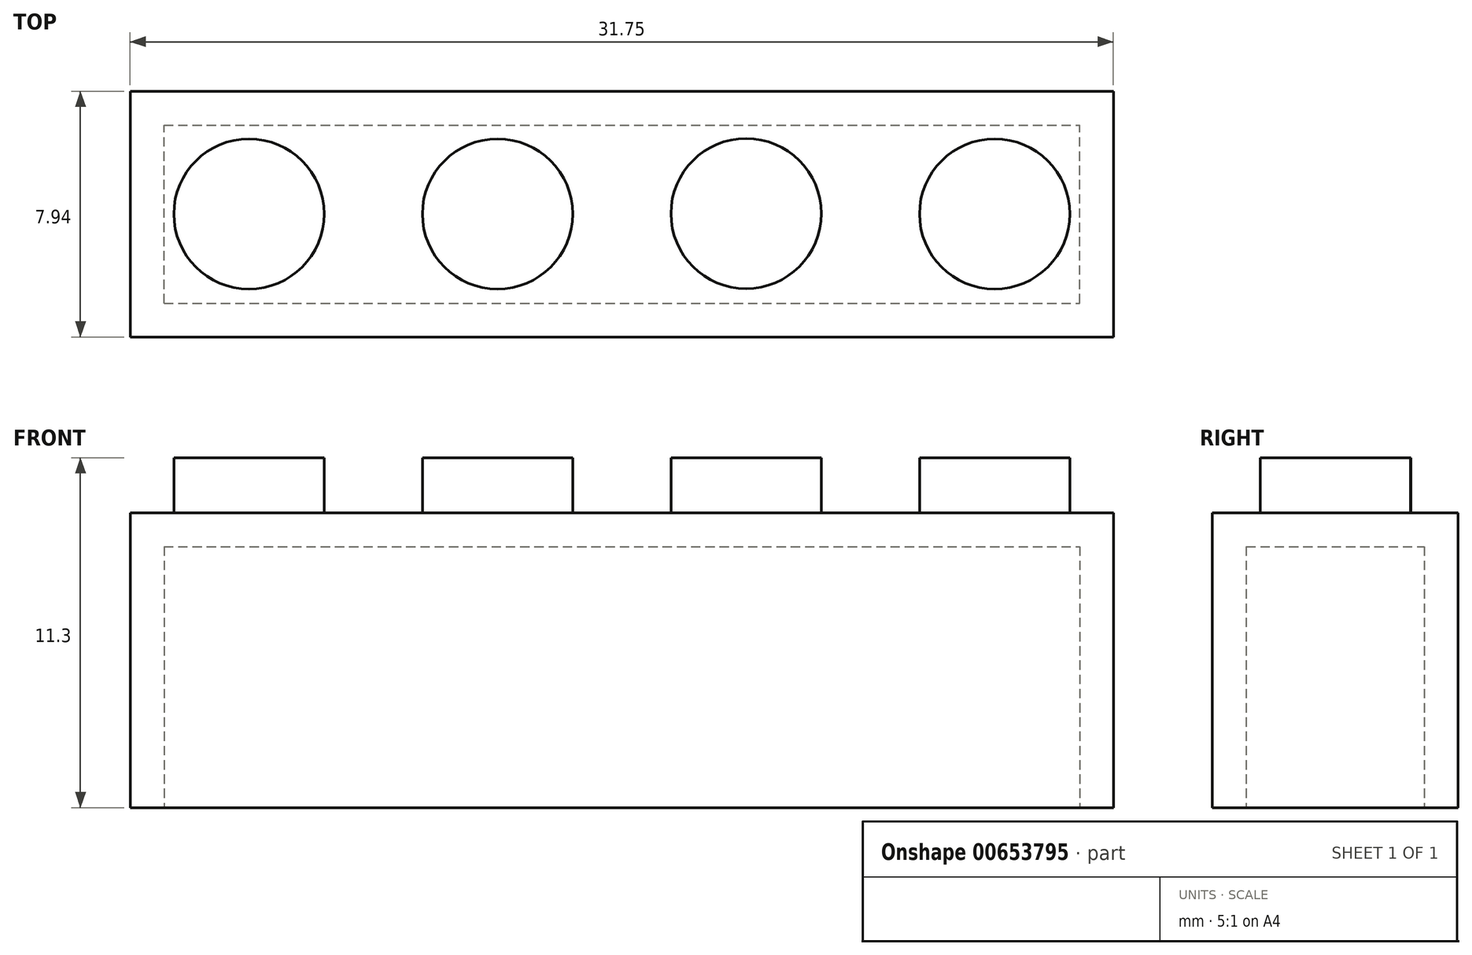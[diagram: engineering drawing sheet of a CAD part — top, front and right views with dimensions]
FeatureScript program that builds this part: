
annotation { "Feature Type Name" : "Feature", "Feature Type Description" : "" }
export const myFeature = defineFeature(function(context is Context, id is Id, definition is map)
    precondition{}
    {
        {
            var Q0;
            Q0=qCreatedBy(makeId("Top.planeOp"),FACE);
            var sketch = newSketch(context, id + "F0", { "sketchPlane" : qUnion([Q0])});
            skLineSegment(sketch, "E0.bottom", {"start": v(-30.69, 19.47) * mm, "end": v(1.06, 19.47) * mm});
            skLineSegment(sketch, "E0.top", {"start": v(-30.69, 11.53) * mm, "end": v(1.06, 11.53) * mm});
            skLineSegment(sketch, "E0.left", {"start": v(-30.69, 19.47) * mm, "end": v(-30.69, 11.53) * mm});
            skLineSegment(sketch, "E0.right", {"start": v(1.06, 19.47) * mm, "end": v(1.06, 11.53) * mm});
            skSolve(sketch);
        }
        {
            var Q0;
            Q0 = qSketchRegion(id + "F0", true);
            extrude(context, id + "F1", {"entities" : qUnion([Q0]), "depth" : 9.52 * mm, "offsetDistance" : 25.4 * mm});
        }
        {
            var Q0;
            Q0=makeQuery(id+"F1.opExtrude","CAP_FACE",FACE,{"disambiguationData":[OSD([sQuery(id+"F0.wireOp",EDGE,"E0.bottom"),sQuery(id+"F0.wireOp",EDGE,"E0.top"),sQuery(id+"F0.wireOp",EDGE,"E0.left"),sQuery(id+"F0.wireOp",EDGE,"E0.right")])],"isStart":false});
            var sketch = newSketch(context, id + "F2", { "sketchPlane" : qUnion([Q0])});
            skCircle(sketch, "E1", {"center": v(-26.85, 15.5) * mm, "radius": 2.43 * mm});
            skCircle(sketch, "E2", {"center": v(-18.83, 15.5) * mm, "radius": 2.43 * mm});
            skCircle(sketch, "E3", {"center": v(-10.8, 15.52) * mm, "radius": 2.43 * mm});
            skCircle(sketch, "E4", {"center": v(-2.77, 15.5) * mm, "radius": 2.43 * mm});
            skSolve(sketch);
        }
        {
            var Q0;
            Q0 = qSketchRegion(id + "F2", true);
            extrude(context, id + "F3", {"entities" : qUnion([Q0]), "operationType" : NewBodyOperationType.ADD, "depth" : 1.78 * mm, "offsetDistance" : 25.4 * mm});
        }
        {
            var Q0;
            Q0=makeQuery(id+"F1.opExtrude","CAP_FACE",FACE,{"disambiguationData":[OSD([sQuery(id+"F0.wireOp",EDGE,"E0.bottom"),sQuery(id+"F0.wireOp",EDGE,"E0.top"),sQuery(id+"F0.wireOp",EDGE,"E0.left"),sQuery(id+"F0.wireOp",EDGE,"E0.right")])],"isStart":true});
            var sketch = newSketch(context, id + "F4", { "sketchPlane" : qUnion([Q0])});
            skSolve(sketch);
        }
        {
            var Q0;
            Q0=makeQuery(id+"F4.imprint","IMPRINT",FACE,{"disambiguationData":[TD([[makeQuery(id+"F4.imprint","IMPRINT",EDGE,{"derivedFrom":makeQuery(id+"F1.opExtrude","CAP_EDGE",EDGE,{"disambiguationData":[OSD([sQuery(id+"F0.wireOp",EDGE,"E0.bottom")])],"isStart":true})}),1.0]])]});
            var sketch = newSketch(context, id + "F5", { "sketchPlane" : qUnion([Q0])});
            skLineSegment(sketch, "E5.bottom", {"start": v(-29.6, -12.62) * mm, "end": v(-0.03, -12.62) * mm});
            skLineSegment(sketch, "E5.top", {"start": v(-29.6, -18.38) * mm, "end": v(-0.03, -18.38) * mm});
            skLineSegment(sketch, "E5.left", {"start": v(-29.6, -12.62) * mm, "end": v(-29.6, -18.38) * mm});
            skLineSegment(sketch, "E5.right", {"start": v(-0.03, -12.62) * mm, "end": v(-0.03, -18.38) * mm});
            skSolve(sketch);
        }
        {
            var Q0;
            Q0 = qSketchRegion(id + "F5", true);
            extrude(context, id + "F6", {"entities" : qUnion([Q0]), "operationType" : NewBodyOperationType.REMOVE, "oppositeDirection" : true, "depth" : 8.43 * mm, "offsetDistance" : 25.4 * mm});
        }
    });
